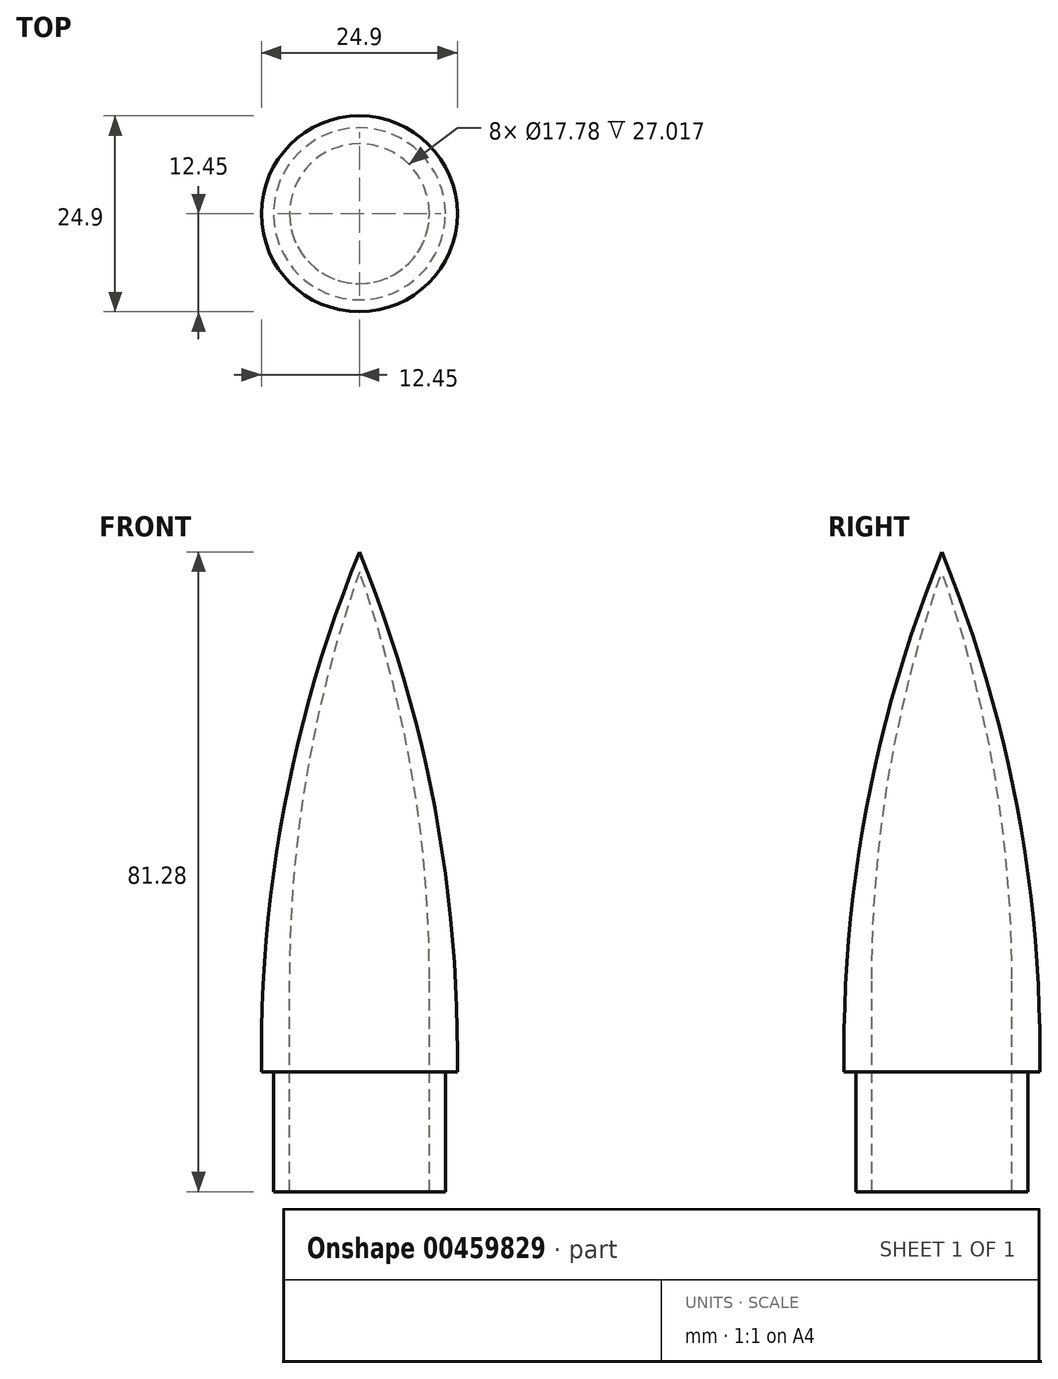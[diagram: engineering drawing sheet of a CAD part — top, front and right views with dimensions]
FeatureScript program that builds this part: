
annotation { "Feature Type Name" : "Feature", "Feature Type Description" : "" }
export const myFeature = defineFeature(function(context is Context, id is Id, definition is map)
    precondition{}
    {
        {
            var Q0;
            Q0=qCreatedBy(makeId("Front.planeOp"),FACE);
            var sketch = newSketch(context, id + "F0", { "sketchPlane" : qUnion([Q0])});
            skLineSegment(sketch, "E0", {"start": v(-10.92, 0) * mm, "end": v(-10.92, 15.24) * mm});
            skLineSegment(sketch, "E1", {"start": v(-10.92, 15.24) * mm, "end": v(-12.45, 15.24) * mm});
            skLineSegment(sketch, "E2", {"start": v(-12.45, 15.24) * mm, "end": v(-12.45, 17.78) * mm});
            skArc(sketch, "E3", {"start": v(-12.45, 17.78) * mm, "mid": v(-9.3, 50.13) * mm, "end": v(0, 81.28) * mm});
            skLineSegment(sketch, "E4", {"start": v(-10.92, 0) * mm, "end": v(-8.9, 0) * mm});
            skLineSegment(sketch, "E5", {"start": v(-8.9, 0) * mm, "end": v(-8.9, 27.02) * mm});
            skLineSegment(sketch, "E6", {"start": v(0, 81.28) * mm, "end": v(0, 78.74) * mm});
            skArc(sketch, "E7", {"start": v(-8.9, 27.02) * mm, "mid": v(-6.65, 53.26) * mm, "end": v(0, 78.74) * mm});
            skSolve(sketch);
        }
        {
            var Q0;
            Q0=makeQuery(id+"F0.imprint","IMPRINT",FACE,{"disambiguationData":[TD([[makeQuery(id+"F0.imprint","IMPRINT",EDGE,{"derivedFrom":sQuery(id+"F0.wireOp",EDGE,"E0")}),-1.0]])]});
            var Q1;
            Q1=sQuery(id+"F0.wireOp",EDGE,"E6");
            revolve(context, id + "F1", {"entities" : qUnion([Q0]), "axis" : qUnion([Q1]), "revolveType" : RevolveType.FULL});
        }
    });
